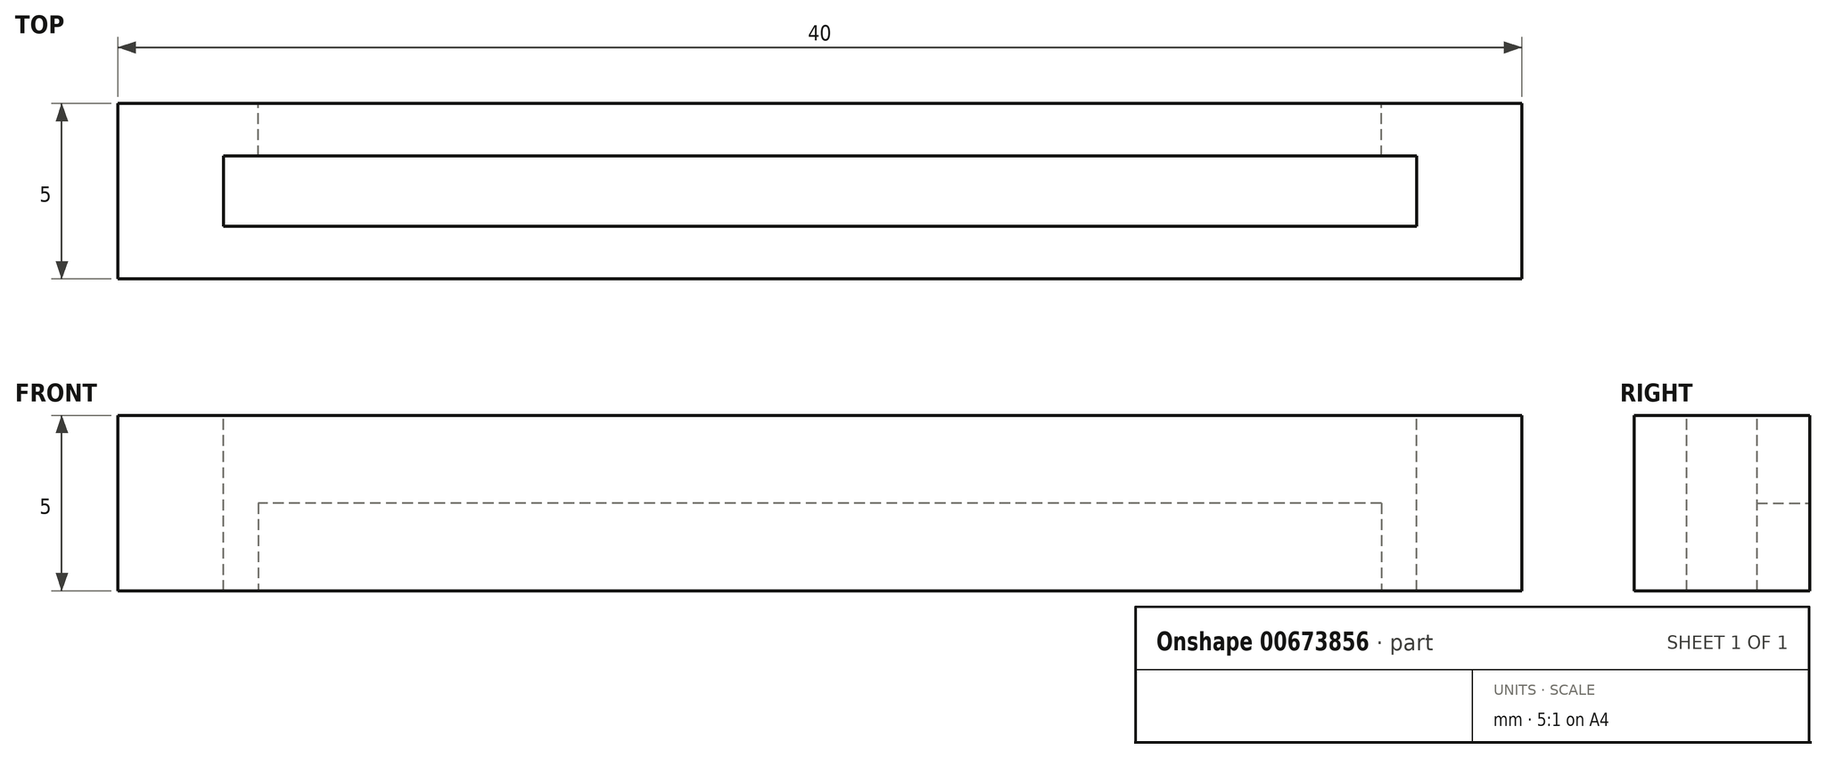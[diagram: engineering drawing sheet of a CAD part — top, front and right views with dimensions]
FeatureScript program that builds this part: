
annotation { "Feature Type Name" : "Feature", "Feature Type Description" : "" }
export const myFeature = defineFeature(function(context is Context, id is Id, definition is map)
    precondition{}
    {
        {
            var Q0;
            Q0=qCreatedBy(makeId("Top.planeOp"),FACE);
            var sketch = newSketch(context, id + "F0", { "sketchPlane" : qUnion([Q0])});
            skLineSegment(sketch, "E0.bottom", {"start": v(-27.12, -32.79) * mm, "end": v(12.88, -32.79) * mm});
            skLineSegment(sketch, "E0.top", {"start": v(-27.12, -37.79) * mm, "end": v(12.88, -37.79) * mm});
            skLineSegment(sketch, "E0.left", {"start": v(-27.12, -32.79) * mm, "end": v(-27.12, -37.79) * mm});
            skLineSegment(sketch, "E0.right", {"start": v(12.88, -32.79) * mm, "end": v(12.88, -37.79) * mm});
            skSolve(sketch);
        }
        {
            var Q0;
            Q0 = qSketchRegion(id + "F0", true);
            extrude(context, id + "F1", {"entities" : qUnion([Q0]), "depth" : 5 * mm, "offsetDistance" : 25 * mm});
        }
        {
            var Q0;
            Q0=makeQuery(id+"F1.opExtrude","CAP_FACE",FACE,{"disambiguationData":[OSD([sQuery(id+"F0.wireOp",EDGE,"E0.bottom"),sQuery(id+"F0.wireOp",EDGE,"E0.top"),sQuery(id+"F0.wireOp",EDGE,"E0.left"),sQuery(id+"F0.wireOp",EDGE,"E0.right")])],"isStart":false});
            var sketch = newSketch(context, id + "F2", { "sketchPlane" : qUnion([Q0])});
            skLineSegment(sketch, "E1.bottom", {"start": v(-24.12, -34.29) * mm, "end": v(9.88, -34.29) * mm});
            skLineSegment(sketch, "E1.top", {"start": v(-24.12, -36.29) * mm, "end": v(9.88, -36.29) * mm});
            skLineSegment(sketch, "E1.left", {"start": v(-24.12, -34.29) * mm, "end": v(-24.12, -36.29) * mm});
            skLineSegment(sketch, "E1.right", {"start": v(9.88, -34.29) * mm, "end": v(9.88, -36.29) * mm});
            skSolve(sketch);
        }
        {
            var Q0;
            Q0 = qSketchRegion(id + "F2", true);
            extrude(context, id + "F3", {"entities" : qUnion([Q0]), "operationType" : NewBodyOperationType.REMOVE, "oppositeDirection" : true, "depth" : 15 * mm, "offsetDistance" : 25 * mm});
        }
        {
            var Q0;
            Q0=makeQuery(id+"F1.opExtrude","SWEPT_FACE",FACE,{"disambiguationData":[OSD([sQuery(id+"F0.wireOp",EDGE,"E0.bottom")])]});
            var sketch = newSketch(context, id + "F4", { "sketchPlane" : qUnion([Q0])});
            skLineSegment(sketch, "E2.bottom", {"start": v(-8.88, 2.5) * mm, "end": v(23.12, 2.5) * mm});
            skLineSegment(sketch, "E2.top", {"start": v(-8.88, -3.5) * mm, "end": v(23.12, -3.5) * mm});
            skLineSegment(sketch, "E2.left", {"start": v(-8.88, 2.5) * mm, "end": v(-8.88, -3.5) * mm});
            skLineSegment(sketch, "E2.right", {"start": v(23.12, 2.5) * mm, "end": v(23.12, -3.5) * mm});
            skSolve(sketch);
        }
        {
            var Q0;
            Q0 = qSketchRegion(id + "F4", true);
            extrude(context, id + "F5", {"entities" : qUnion([Q0]), "operationType" : NewBodyOperationType.REMOVE, "oppositeDirection" : true, "depth" : 2 * mm, "offsetDistance" : 25 * mm});
        }
    });
